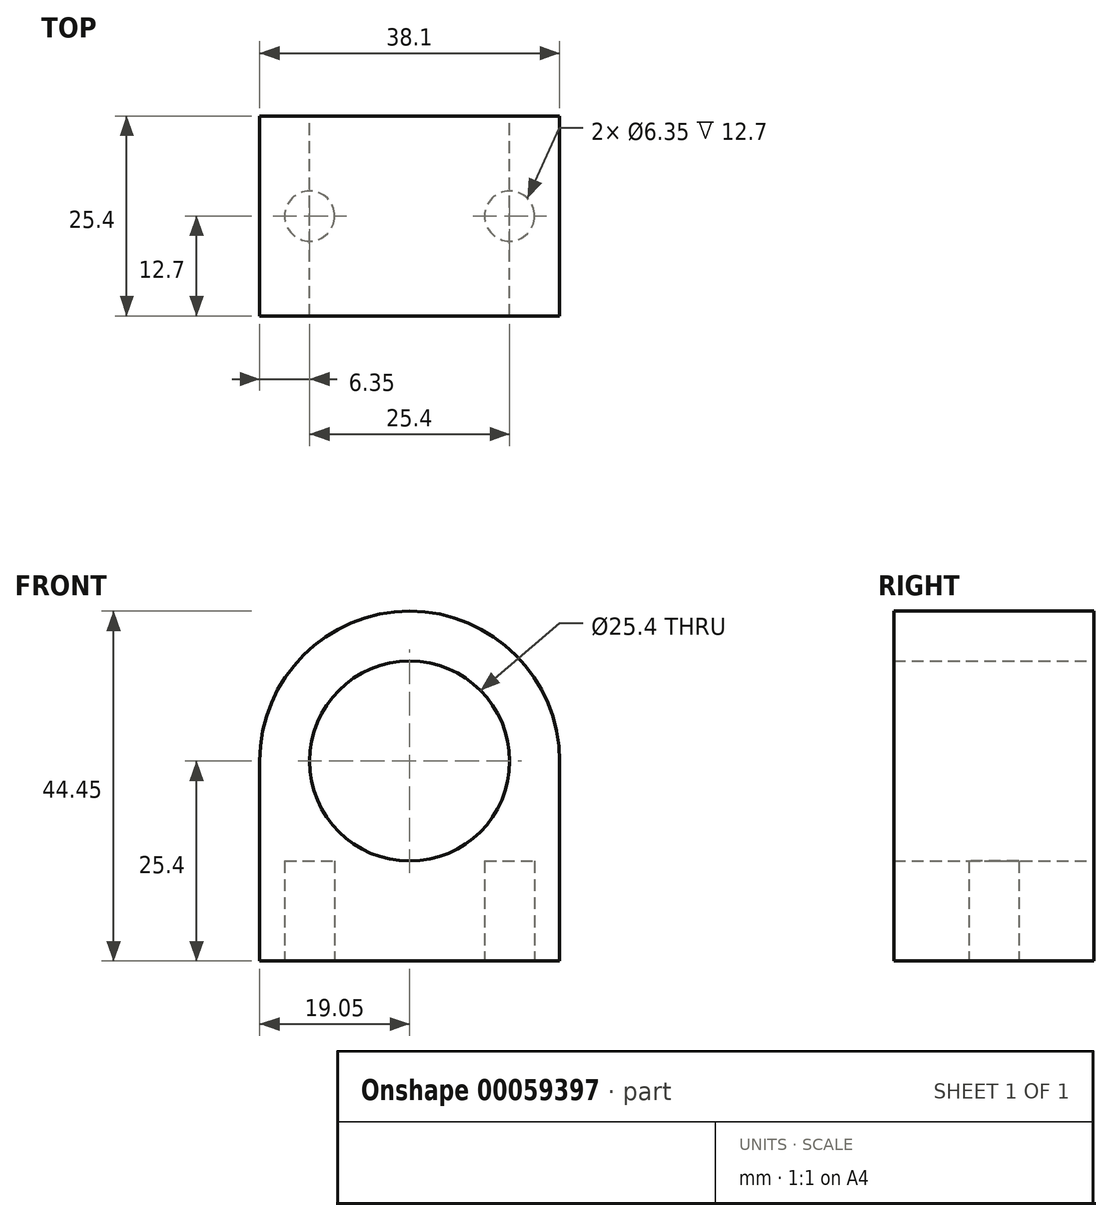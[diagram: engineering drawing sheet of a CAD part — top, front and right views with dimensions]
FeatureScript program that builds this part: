
annotation { "Feature Type Name" : "Feature", "Feature Type Description" : "" }
export const myFeature = defineFeature(function(context is Context, id is Id, definition is map)
    precondition{}
    {
        {
            var Q0;
            Q0=qCreatedBy(makeId("Front.planeOp"),FACE);
            var sketch = newSketch(context, id + "F0", { "sketchPlane" : qUnion([Q0])});
            skCircle(sketch, "E0", {"center": v(0, 0) * mm, "radius": 12.7 * mm});
            skArc(sketch, "E1", {"start": v(19.05, 0) * mm, "mid": v(0, 19.05) * mm, "end": v(-19.05, 0) * mm});
            skLineSegment(sketch, "E2", {"start": v(-19.05, 0) * mm, "end": v(-19.05, -25.4) * mm});
            skLineSegment(sketch, "E3", {"start": v(-19.05, -25.4) * mm, "end": v(19.05, -25.4) * mm});
            skLineSegment(sketch, "E4", {"start": v(19.05, 0) * mm, "end": v(19.05, -25.4) * mm});
            skSolve(sketch);
        }
        {
            var Q0;
            Q0 = qSketchRegion(id + "F0", true);
            extrude(context, id + "F1", {"entities" : qUnion([Q0]), "depth" : 25.4 * mm});
        }
        {
            var Q0;
            Q0=makeQuery(id+"F1.opExtrude","SWEPT_FACE",FACE,{"disambiguationData":[OSD([sQuery(id+"F0.wireOp",EDGE,"E3")])]});
            var sketch = newSketch(context, id + "F2", { "sketchPlane" : qUnion([Q0])});
            skLineSegment(sketch, "E5", {"start": v(-25.02, 12.7) * mm, "end": v(25.43, 12.7) * mm, "construction": true});
            skPoint(sketch, "E5.startSnap0", {"position": v(-19.05, 12.7) * mm});
            skCircle(sketch, "E6", {"center": v(-12.7, 12.7) * mm, "radius": 3.18 * mm});
            skCircle(sketch, "E7", {"center": v(12.7, 12.7) * mm, "radius": 3.18 * mm});
            skSolve(sketch);
        }
        {
            var Q0;
            Q0 = qSketchRegion(id + "F2", true);
            extrude(context, id + "F3", {"entities" : qUnion([Q0]), "operationType" : NewBodyOperationType.REMOVE, "oppositeDirection" : true, "depth" : 12.7 * mm});
        }
    });
